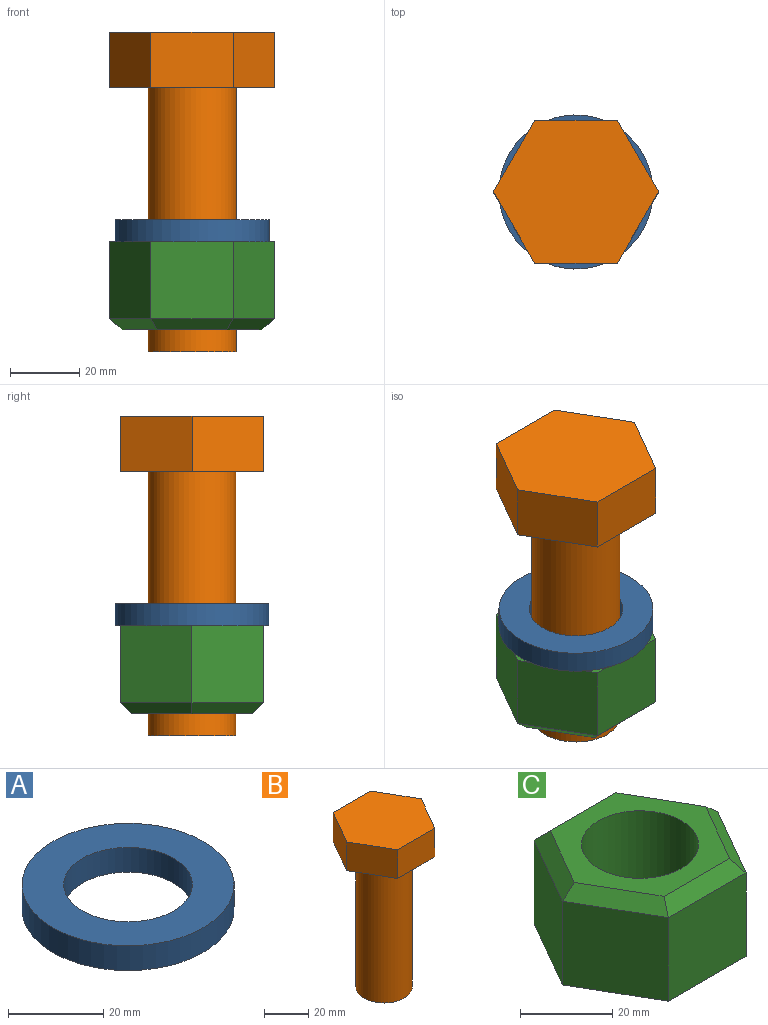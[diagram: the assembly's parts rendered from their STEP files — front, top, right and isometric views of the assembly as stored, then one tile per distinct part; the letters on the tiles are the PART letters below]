
ASSEMBLY  parts=3 mates=2
PART A: 4 faces, bbox 44.5x44.5x6.4 mm
  f0: cylinder r=13.49mm len=26.99mm, axis (0,0,-1), area 538.4mm2, adj f2,f3
  f1: cylinder r=22.23mm len=44.45mm, axis (0,0,-1), area 886.7mm2, adj f2,f3
  f2: plane 44.45x44.45mm, normal (0,0,1), area 979.8mm2, adj f0,f1
  f3: plane 44.45x44.45mm, normal (0,0,-1), area 979.8mm2, adj f0,f1
PART B: 10 faces, bbox 47.7x41.3x92.1 mm
  f0: cylinder r=12.7mm len=76.2mm, axis (0,0,1), area 6080.5mm2, adj f1,f9
  f1: plane 25.4x25.4mm, normal (0,0,-1), area 506.7mm2, adj f0
  f2: plane 20.64x15.88mm, normal (-0.87,0.5,0), area 378.3mm2, adj f3,f7,f8,f9
  f3: plane 20.64x15.88mm, normal (-0.87,-0.5,0), area 378.3mm2, adj f2,f4,f8,f9
  f4: plane 23.83x15.88mm, normal (0,-1,0), area 378.3mm2, adj f3,f5,f8,f9
  f5: plane 20.64x15.88mm, normal (0.87,-0.5,0), area 378.3mm2, adj f4,f6,f8,f9
  f6: plane 20.64x15.88mm, normal (0.87,0.5,0), area 378.3mm2, adj f5,f7,f8,f9
  f7: plane 23.83x15.88mm, normal (0,1,0), area 378.3mm2, adj f2,f6,f8,f9
  f8: plane 47.66x41.28mm, normal (0,0,1), area 1475.4mm2, adj f2,f3,f4,f5,f6,f7
  f9: plane 47.66x41.28mm, normal (0,0,-1), area 968.7mm2, adj f0,f2,f3,f4,f5,f6,f7
PART C: 15 faces, bbox 47.7x41.3x25.4 mm
  f0: plane 22.23x20.64mm, normal (-0.87,0.5,0), area 529.6mm2, adj f1,f6,f8,f9
  f1: plane 22.23x20.64mm, normal (-0.87,-0.5,0), area 529.6mm2, adj f0,f2,f8,f11
  f2: plane 23.83x22.23mm, normal (0,-1,0), area 529.6mm2, adj f1,f3,f8,f13
  f3: plane 22.23x20.64mm, normal (0.87,-0.5,0), area 529.6mm2, adj f2,f4,f8,f14
  f4: plane 22.23x20.64mm, normal (0.87,0.5,0), area 529.6mm2, adj f3,f6,f8,f12
  f5: cylinder r=12.7mm len=25.4mm, axis (0,0,-1), area 2026.8mm2, adj f7,f8
  f6: plane 23.83x22.23mm, normal (0,1,0), area 529.6mm2, adj f0,f4,f8,f10
  f7: plane 40.33x34.93mm, normal (0,0,1), area 549.6mm2, adj f5,f9,f10,f11,f12,f13,f14
  f8: plane 47.66x41.28mm, normal (0,0,-1), area 968.7mm2, adj f0,f1,f2,f3,f4,f5,f6
  f9: plane 20.64x13.75mm, normal (-0.61,0.35,0.71), area 98.8mm2, adj f0,f7,f10,f11
  f10: plane 23.83x3.18mm, normal (0,0.71,0.71), area 98.8mm2, adj f6,f7,f9,f12
  f11: plane 20.64x13.75mm, normal (-0.61,-0.35,0.71), area 98.8mm2, adj f1,f7,f9,f13
  f12: plane 20.64x13.75mm, normal (0.61,0.35,0.71), area 98.8mm2, adj f4,f7,f10,f14
  f13: plane 23.83x3.18mm, normal (0,-0.71,0.71), area 98.8mm2, adj f2,f7,f11,f14
  f14: plane 20.64x13.75mm, normal (0.61,-0.35,0.71), area 98.8mm2, adj f3,f7,f12,f13
PLACE A t=(-11.99,-14.74,-32.36)mm
PLACE B t=(-11.99,-14.74,12.09)mm
PLACE C rot(axis=(1,0,0),180deg) t=(-11.99,-14.74,-32.36)mm
MATE fastened A.f0 <-> C.f5  axis (0,0,-1) through (-11.99,-14.74,-32.36)mm
MATE fastened C.f5 <-> B.f0  axis (0,0,-1) through (-11.99,-14.74,-57.76)mm
